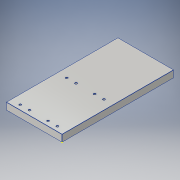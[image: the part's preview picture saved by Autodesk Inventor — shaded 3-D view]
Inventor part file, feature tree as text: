
AUTODESK INVENTOR PART (.ipt)
format: ipt  version: 2016 (Build 200138000, 138)  size: 162,304 bytes
history: native  units: in
note: dims shown in document units (in); Inventor stores cm internally (conversion verified against a paired STEP export)
features: sketch x3, extrude x3, plane x1, pattern_linear x1, mirror x1, chamfer x1
ambient origin geometry x8: Origin, YZ Plane, XZ Plane, XY Plane, X Axis, Y Axis, Z Axis, Center Point
bodies: Solid1 (feature_tree)
feature tree (10):
  sketch  "Sketch1"  dims[d0=6.0in d1=3.0in]
  extrude  "Extrusion1"  Depth=3.0in
  sketch  "Sketch4"  dims[d8=0.1in d9=0.5in d10=0.5in d11=0.25in d12=0.1875in d13=0.0in d14=0.1in d15=0.1875in d16=0.0in d29=0.7874in d31=2.5in d32=0.01in d33=0.125in d34=45.0deg]
  extrude  "Extrusion2"  Depth=0.375in
  extrude  "Extrusion3"  Depth=0.1875in
  plane  "Work Plane1"
  pattern_linear  "Rectangular Pattern3"  Spacing1=0.5in  [1 undecoded]
  mirror  "Mirror1"
  chamfer  "Chamfer1"  Distance=0.25in
  sketch  "Sketch2"  dims[d2=0.375in d3=0.0in d7=0.325in]
note: 1 required parameter value undecoded (feature->parameter linkage not recoverable at this tier; creation-order binding heuristic only, values carry confidence <= 0.55)
